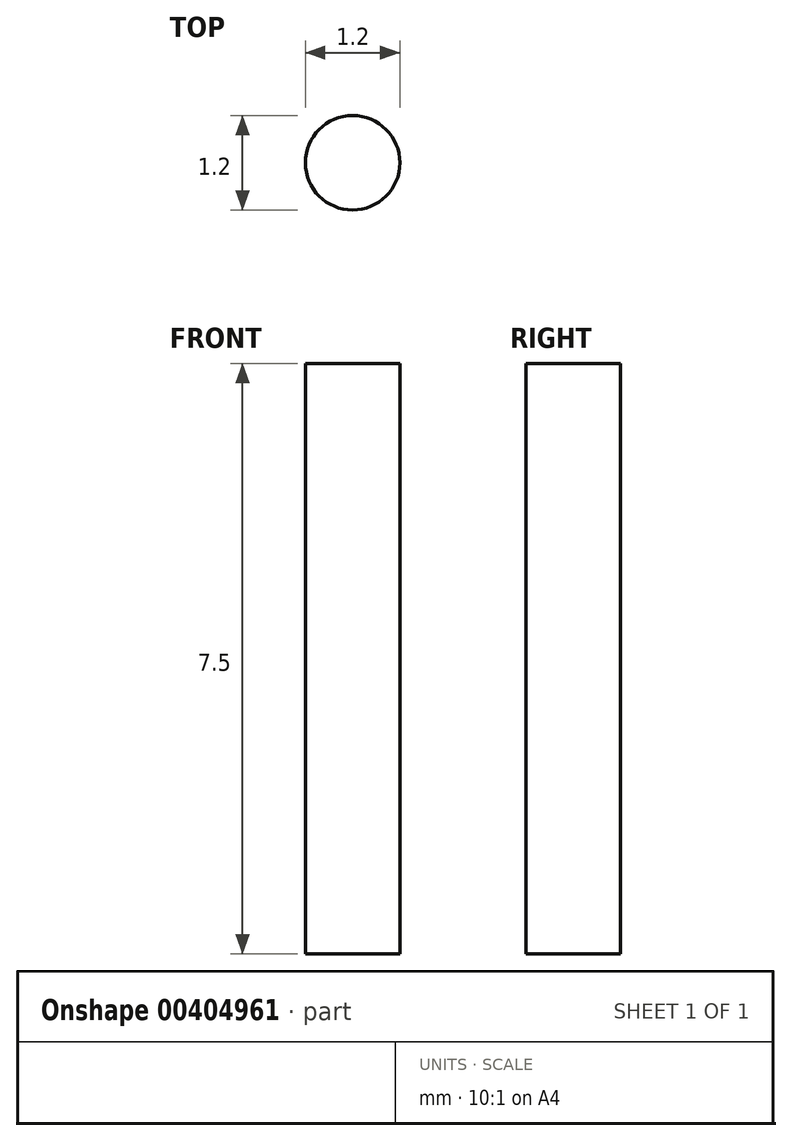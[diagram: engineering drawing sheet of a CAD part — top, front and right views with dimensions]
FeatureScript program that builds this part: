
annotation { "Feature Type Name" : "Feature", "Feature Type Description" : "" }
export const myFeature = defineFeature(function(context is Context, id is Id, definition is map)
    precondition{}
    {
        {
            var Q0;
            Q0=qCreatedBy(makeId("Top.planeOp"),FACE);
            var sketch = newSketch(context, id + "F0", { "sketchPlane" : qUnion([Q0])});
            skCircle(sketch, "E0", {"center": v(0, 0) * mm, "radius": 0.6 * mm});
            skSolve(sketch);
        }
        {
            var Q0;
            Q0=qSketchRegion(id+"F0",true);
            extrude(context, id + "F1", {"entities" : qUnion([Q0]), "depth" : 7.5 * mm});
        }
    });
